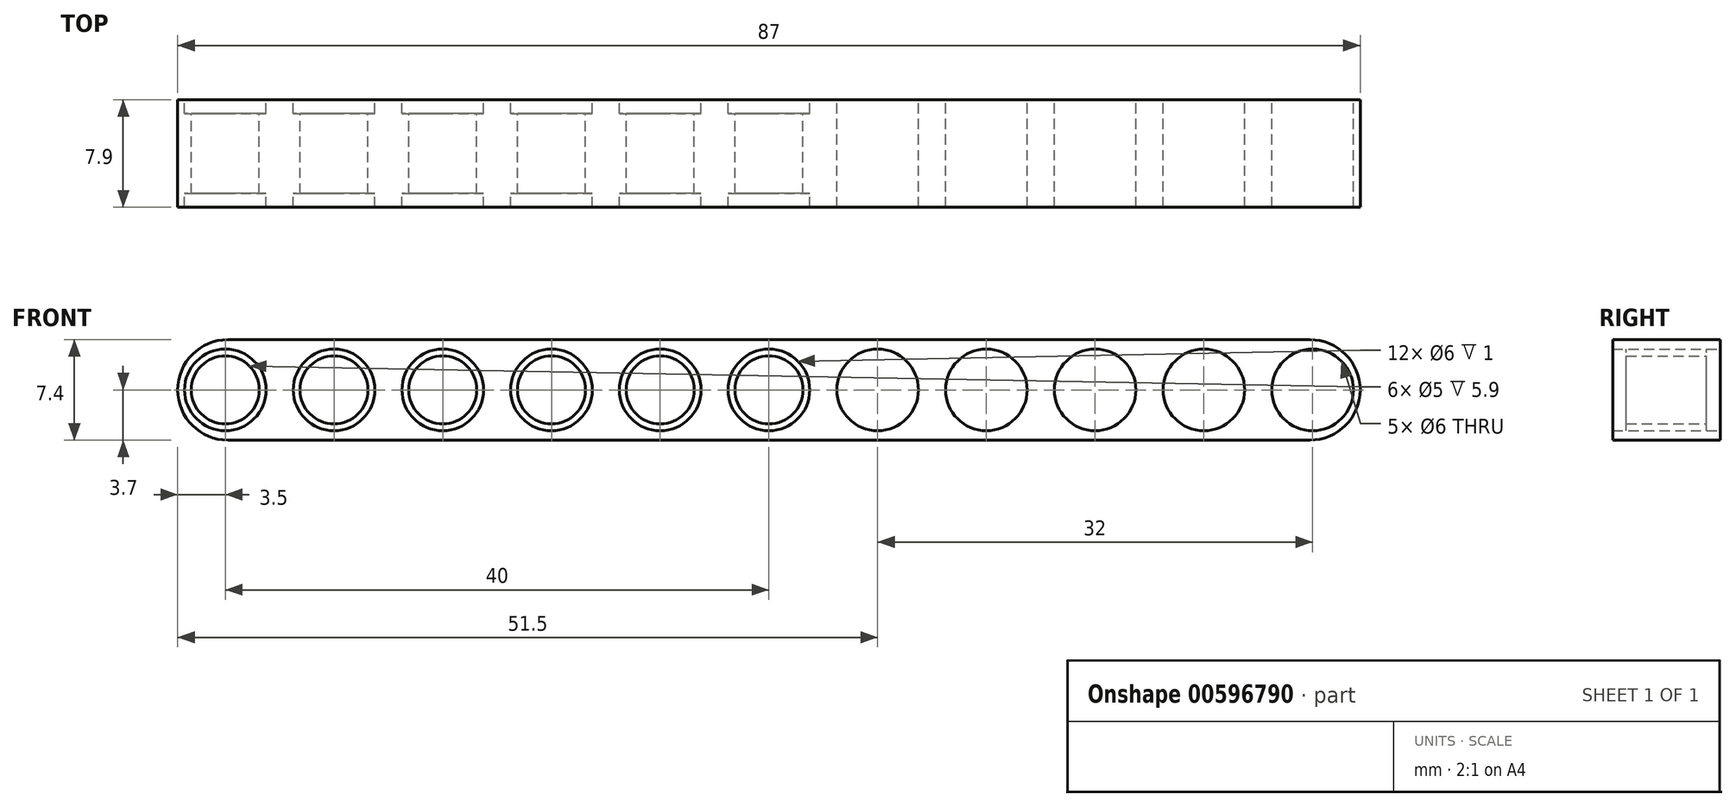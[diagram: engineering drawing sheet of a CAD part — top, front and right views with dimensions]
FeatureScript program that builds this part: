
annotation { "Feature Type Name" : "Feature", "Feature Type Description" : "" }
export const myFeature = defineFeature(function(context is Context, id is Id, definition is map)
    precondition{}
    {
        {
            var Q0;
            Q0=qCreatedBy(makeId("Front.planeOp"),FACE);
            var sketch = newSketch(context, id + "F0", { "sketchPlane" : qUnion([Q0])});
            skLineSegment(sketch, "E0.bottom", {"start": v(43.5, 3.7) * mm, "end": v(-43.5, 3.7) * mm});
            skLineSegment(sketch, "E0.top", {"start": v(43.5, -3.7) * mm, "end": v(-43.5, -3.7) * mm});
            skLineSegment(sketch, "E0.left", {"start": v(43.5, 3.7) * mm, "end": v(43.5, -3.7) * mm});
            skLineSegment(sketch, "E0.right", {"start": v(-43.5, 3.7) * mm, "end": v(-43.5, -3.7) * mm});
            skPoint(sketch, "E0.middle", {"position": v(0, 0) * mm});
            skCircle(sketch, "E1", {"center": v(0, 0) * mm, "radius": 2.5 * mm});
            skCircle(sketch, "E2", {"center": v(0, 0) * mm, "radius": 3 * mm});
            skCircle(sketch, "E3", {"center": v(-8, 0) * mm, "radius": 2.5 * mm});
            skCircle(sketch, "E4", {"center": v(-8, 0) * mm, "radius": 3 * mm});
            skCircle(sketch, "E5", {"center": v(-16, 0) * mm, "radius": 2.5 * mm});
            skCircle(sketch, "E6", {"center": v(-16, 0) * mm, "radius": 3 * mm});
            skCircle(sketch, "E7", {"center": v(-24, 0) * mm, "radius": 2.5 * mm});
            skCircle(sketch, "E8", {"center": v(-24, 0) * mm, "radius": 3 * mm});
            skCircle(sketch, "E9", {"center": v(-32, 0) * mm, "radius": 2.5 * mm});
            skCircle(sketch, "E10", {"center": v(-32, 0) * mm, "radius": 3 * mm});
            skCircle(sketch, "E11", {"center": v(-40, 0) * mm, "radius": 2.5 * mm});
            skCircle(sketch, "E12", {"center": v(-40, 0) * mm, "radius": 3 * mm});
            skLineSegment(sketch, "E13", {"start": v(0, 8.5) * mm, "end": v(0, -10.33) * mm, "construction": true});
            skCircle(sketch, "E14.MirrorC", {"center": v(8, 0) * mm, "radius": 3 * mm});
            skCircle(sketch, "E15.MirrorC", {"center": v(8, 0) * mm, "radius": 2.5 * mm});
            skCircle(sketch, "E16.MirrorC", {"center": v(16, 0) * mm, "radius": 3 * mm});
            skCircle(sketch, "E17.MirrorC", {"center": v(16, 0) * mm, "radius": 2.5 * mm});
            skCircle(sketch, "E18.MirrorC", {"center": v(24, 0) * mm, "radius": 3 * mm});
            skCircle(sketch, "E19.MirrorC", {"center": v(24, 0) * mm, "radius": 2.5 * mm});
            skCircle(sketch, "E20.MirrorC", {"center": v(32, 0) * mm, "radius": 3 * mm});
            skCircle(sketch, "E21.MirrorC", {"center": v(32, 0) * mm, "radius": 2.5 * mm});
            skCircle(sketch, "E22.MirrorC", {"center": v(40, 0) * mm, "radius": 3 * mm});
            skCircle(sketch, "E23.MirrorC", {"center": v(40, 0) * mm, "radius": 2.5 * mm});
            skSolve(sketch);
        }
        {
            var Q0;
            Q0=makeQuery(id+"F0.imprint","IMPRINT",FACE,{"disambiguationData":[TD([[makeQuery(id+"F0.imprint","IMPRINT",EDGE,{"derivedFrom":sQuery(id+"F0.wireOp",EDGE,"E0.bottom")}),1.0]])]});
            extrude(context, id + "F1", {"entities" : qUnion([Q0]), "endBound" : BoundingType.SYMMETRIC, "depth" : 7.9 * mm, "offsetDistance" : 25 * mm});
        }
        {
            var Q0;
            Q0=makeQuery(id+"F0.imprint","IMPRINT",FACE,{"disambiguationData":[TD([[makeQuery(id+"F0.imprint","IMPRINT",EDGE,{"derivedFrom":sQuery(id+"F0.wireOp",EDGE,"E11")}),-1.0]])]});
            var Q1;
            Q1=makeQuery(id+"F0.imprint","IMPRINT",FACE,{"disambiguationData":[TD([[makeQuery(id+"F0.imprint","IMPRINT",EDGE,{"derivedFrom":sQuery(id+"F0.wireOp",EDGE,"E9")}),-1.0]])]});
            var Q2;
            Q2=makeQuery(id+"F0.imprint","IMPRINT",FACE,{"disambiguationData":[TD([[makeQuery(id+"F0.imprint","IMPRINT",EDGE,{"derivedFrom":sQuery(id+"F0.wireOp",EDGE,"E7")}),-1.0]])]});
            var Q3;
            Q3=makeQuery(id+"F0.imprint","IMPRINT",FACE,{"disambiguationData":[TD([[makeQuery(id+"F0.imprint","IMPRINT",EDGE,{"derivedFrom":sQuery(id+"F0.wireOp",EDGE,"E5")}),-1.0]])]});
            var Q4;
            Q4=makeQuery(id+"F0.imprint","IMPRINT",FACE,{"disambiguationData":[TD([[makeQuery(id+"F0.imprint","IMPRINT",EDGE,{"derivedFrom":sQuery(id+"F0.wireOp",EDGE,"E3")}),-1.0]])]});
            var Q5;
            Q5=makeQuery(id+"F0.imprint","IMPRINT",FACE,{"disambiguationData":[TD([[makeQuery(id+"F0.imprint","IMPRINT",EDGE,{"derivedFrom":sQuery(id+"F0.wireOp",EDGE,"E1")}),-1.0]])]});
            var Q6;
            Q6=makeQuery(id+"F0.imprint","IMPRINT",FACE,{"disambiguationData":[TD([[makeQuery(id+"F0.imprint","IMPRINT",EDGE,{"derivedFrom":sQuery(id+"F0.wireOp",EDGE,"E14.MirrorC")}),-1.0]])]});
            var Q7;
            Q7=makeQuery(id+"F0.imprint","IMPRINT",FACE,{"disambiguationData":[TD([[makeQuery(id+"F0.imprint","IMPRINT",EDGE,{"derivedFrom":sQuery(id+"F0.wireOp",EDGE,"E16.MirrorC")}),-1.0]])]});
            var Q8;
            Q8=makeQuery(id+"F0.imprint","IMPRINT",FACE,{"disambiguationData":[TD([[makeQuery(id+"F0.imprint","IMPRINT",EDGE,{"derivedFrom":sQuery(id+"F0.wireOp",EDGE,"E18.MirrorC")}),-1.0]])]});
            var Q9;
            Q9=makeQuery(id+"F0.imprint","IMPRINT",FACE,{"disambiguationData":[TD([[makeQuery(id+"F0.imprint","IMPRINT",EDGE,{"derivedFrom":sQuery(id+"F0.wireOp",EDGE,"E20.MirrorC")}),-1.0]])]});
            var Q10;
            Q10=makeQuery(id+"F0.imprint","IMPRINT",FACE,{"disambiguationData":[TD([[makeQuery(id+"F0.imprint","IMPRINT",EDGE,{"derivedFrom":sQuery(id+"F0.wireOp",EDGE,"E22.MirrorC")}),-1.0]])]});
            extrude(context, id + "F2", {"entities" : qUnion([Q0, Q1, Q2, Q3, Q4, Q5, Q6, Q7, Q8, Q9, Q10]), "operationType" : NewBodyOperationType.ADD, "endBound" : BoundingType.SYMMETRIC, "depth" : 5.9 * mm, "offsetDistance" : 25 * mm});
        }
        {
            var Q0;
            Q0=makeQuery(id+"F1.opExtrude","SWEPT_EDGE",EDGE,{"disambiguationData":[OSD([sQuery(id+"F0.wireOp",EDGE,"E0.bottom"),sQuery(id+"F0.wireOp",EDGE,"E0.right")])]});
            var Q1;
            Q1=makeQuery(id+"F1.opExtrude","SWEPT_EDGE",EDGE,{"disambiguationData":[OSD([sQuery(id+"F0.wireOp",EDGE,"E0.top"),sQuery(id+"F0.wireOp",EDGE,"E0.right")])]});
            var Q2;
            Q2=makeQuery(id+"F1.opExtrude","SWEPT_EDGE",EDGE,{"disambiguationData":[OSD([sQuery(id+"F0.wireOp",EDGE,"E0.bottom"),sQuery(id+"F0.wireOp",EDGE,"E0.left")])]});
            var Q3;
            Q3=makeQuery(id+"F1.opExtrude","SWEPT_EDGE",EDGE,{"disambiguationData":[OSD([sQuery(id+"F0.wireOp",EDGE,"E0.top"),sQuery(id+"F0.wireOp",EDGE,"E0.left")])]});
            fillet(context, id + "F3", {"entities" : qUnion([Q0, Q1, Q2, Q3]), "radius" : 3.7 * mm, "tangentPropagation" : true, "allowEdgeOverflow" : false});
        }
    });
